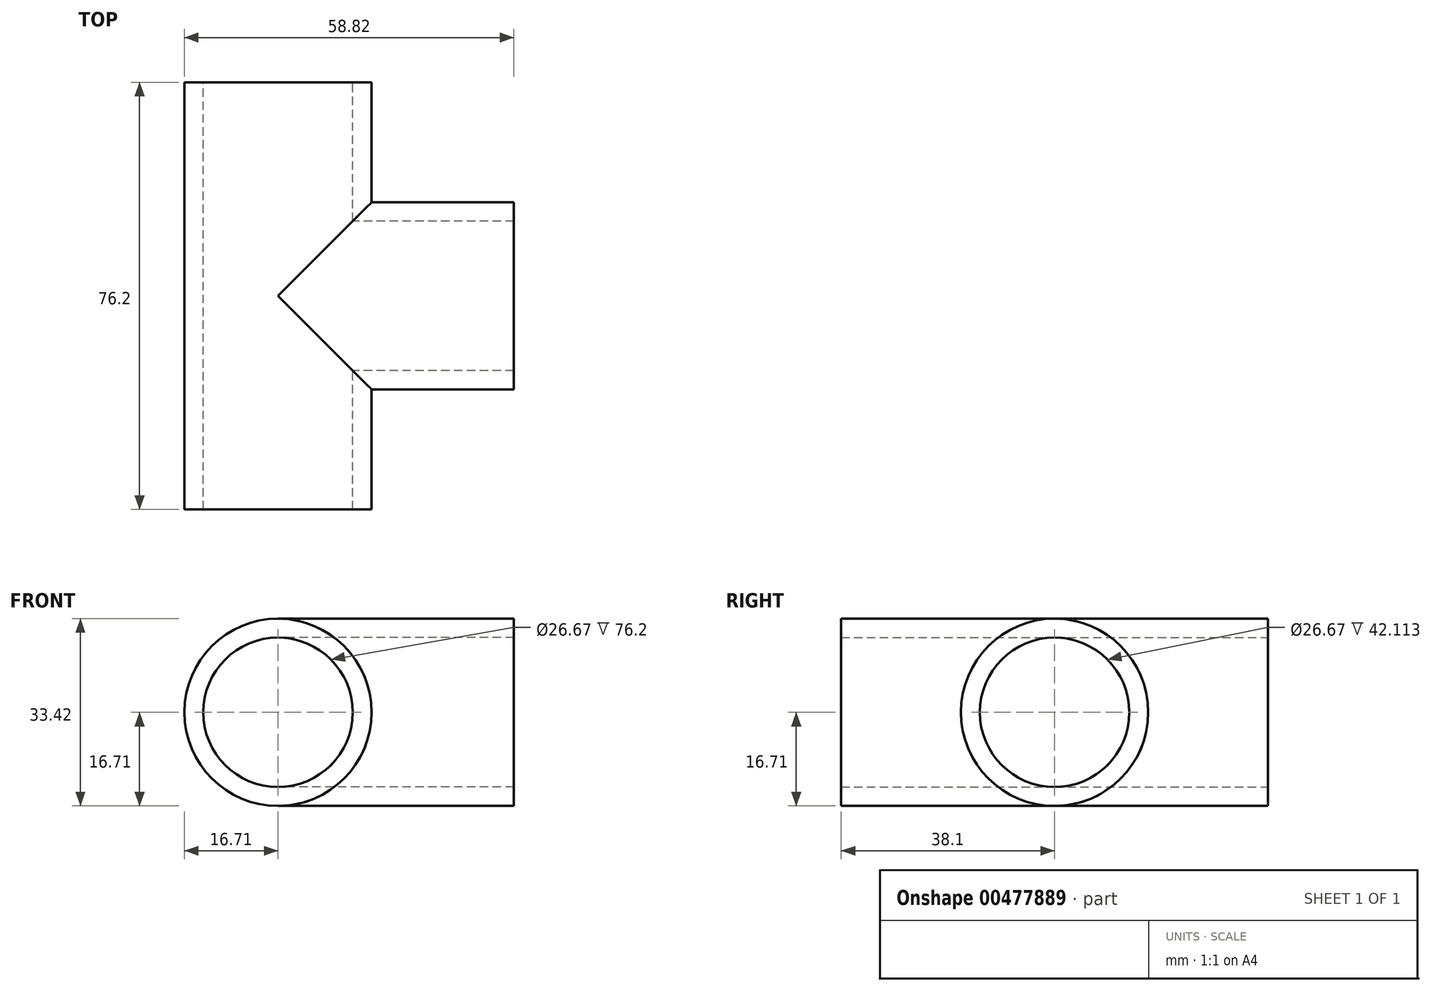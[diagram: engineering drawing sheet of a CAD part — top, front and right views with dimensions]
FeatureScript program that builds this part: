
annotation { "Feature Type Name" : "Feature", "Feature Type Description" : "" }
export const myFeature = defineFeature(function(context is Context, id is Id, definition is map)
    precondition{}
    {
        {
            var Q0;
            Q0=qCreatedBy(makeId("Top.planeOp"),FACE);
            var sketch = newSketch(context, id + "F0", { "sketchPlane" : qUnion([Q0])});
            skLineSegment(sketch, "E0", {"start": v(0, 38.1) * mm, "end": v(0, 0) * mm});
            skLineSegment(sketch, "E1", {"start": v(0, 0) * mm, "end": v(0, -38.1) * mm});
            skLineSegment(sketch, "E2", {"start": v(0, 0) * mm, "end": v(42.11, 0) * mm});
            skLineSegment(sketch, "E3", {"start": v(42.11, 0) * mm, "end": v(42.11, 16.71) * mm});
            skLineSegment(sketch, "E4", {"start": v(42.11, 16.71) * mm, "end": v(16.71, 16.71) * mm});
            skLineSegment(sketch, "E5", {"start": v(16.71, 16.71) * mm, "end": v(16.71, 38.1) * mm});
            skLineSegment(sketch, "E6", {"start": v(16.71, 38.1) * mm, "end": v(-16.71, 38.1) * mm});
            skLineSegment(sketch, "E7", {"start": v(-16.71, 38.1) * mm, "end": v(-16.71, -38.1) * mm});
            skLineSegment(sketch, "E8", {"start": v(-16.71, -38.1) * mm, "end": v(16.71, -38.1) * mm});
            skLineSegment(sketch, "E9", {"start": v(16.71, -38.1) * mm, "end": v(16.71, -16.71) * mm});
            skLineSegment(sketch, "E10", {"start": v(16.71, -16.71) * mm, "end": v(42.11, -16.71) * mm});
            skLineSegment(sketch, "E11", {"start": v(42.11, -16.71) * mm, "end": v(42.11, 0) * mm});
            skLineSegment(sketch, "E12", {"start": v(16.71, 16.71) * mm, "end": v(0, 16.71) * mm});
            skPoint(sketch, "E12.endSnap0", {"position": v(0, 19.05) * mm});
            skLineSegment(sketch, "E13", {"start": v(16.71, -16.71) * mm, "end": v(0, -16.71) * mm});
            skLineSegment(sketch, "E14", {"start": v(0, 16.71) * mm, "end": v(-16.71, 16.71) * mm, "construction": true});
            skLineSegment(sketch, "E15", {"start": v(42.11, 13.33) * mm, "end": v(3.29, 13.33) * mm});
            skLineSegment(sketch, "E16", {"start": v(42.11, -13.34) * mm, "end": v(3.29, -13.34) * mm});
            skLineSegment(sketch, "E17", {"start": v(-13.33, -38.1) * mm, "end": v(-13.33, 38.1) * mm});
            skLineSegment(sketch, "E18", {"start": v(3.29, 13.33) * mm, "end": v(0, 13.33) * mm});
            skLineSegment(sketch, "E19", {"start": v(3.29, -13.34) * mm, "end": v(0, -13.34) * mm});
            skLineSegment(sketch, "E20", {"start": v(13.34, 16.71) * mm, "end": v(13.34, 38.1) * mm, "construction": true});
            skLineSegment(sketch, "E21", {"start": v(13.34, -16.71) * mm, "end": v(13.34, -38.1) * mm, "construction": true});
            skLineSegment(sketch, "E22", {"start": v(13.34, -27.4) * mm, "end": v(16.71, -27.4) * mm, "construction": true});
            skLineSegment(sketch, "E23", {"start": v(16.71, 27.4) * mm, "end": v(13.33, 27.4) * mm, "construction": true});
            skLineSegment(sketch, "E24", {"start": v(-13.33, 27.4) * mm, "end": v(-16.71, 27.4) * mm, "construction": true});
            skLineSegment(sketch, "E25", {"start": v(29.41, 16.71) * mm, "end": v(29.41, 13.33) * mm, "construction": true});
            skLineSegment(sketch, "E26", {"start": v(29.41, -16.71) * mm, "end": v(29.41, -13.33) * mm, "construction": true});
            skSolve(sketch);
        }
        {
            var Q0;
            {var subQ0=sQuery(id+"F0.wireOp",EDGE,"E7");Q0=makeQuery(id+"F0.imprint","IMPRINT",FACE,{"disambiguationData":[TD([[makeQuery(id+"F0.imprint","IMPRINT",EDGE,{"derivedFrom":subQ0}),1.0]])]});}
            var Q1;
            Q1=sQuery(id+"F0.wireOp",EDGE,"E0");
            revolve(context, id + "F1", {"entities" : qUnion([Q0]), "axis" : qUnion([Q1]), "revolveType" : RevolveType.FULL});
        }
        {
            var Q0;
            {var subQ1=sQuery(id+"F0.wireOp",EDGE,"E4");Q0=makeQuery(id+"F0.imprint","IMPRINT",FACE,{"disambiguationData":[TD([[makeQuery(id+"F0.imprint","IMPRINT",EDGE,{"derivedFrom":subQ1}),1.0]])]});}
            var Q1;
            Q1=sQuery(id+"F0.wireOp",EDGE,"E2");
            revolve(context, id + "F2", {"operationType" : NewBodyOperationType.ADD, "entities" : qUnion([Q0]), "axis" : qUnion([Q1]), "revolveType" : RevolveType.FULL});
        }
        {
            var Q0;
            Q0=makeQuery(id+"F2.opRevolve","SWEPT_FACE",FACE,{"disambiguationData":[OSD([sQuery(id+"F0.wireOp",EDGE,"E3")])]});
            var sketch = newSketch(context, id + "F3", { "sketchPlane" : qUnion([Q0])});
            skSolve(sketch);
        }
        {
            var Q0;
            Q0=makeQuery(id+"F1.opRevolve","SWEPT_FACE",FACE,{"disambiguationData":[OSD([sQuery(id+"F0.wireOp",EDGE,"E8")])]});
            var sketch = newSketch(context, id + "F4", { "sketchPlane" : qUnion([Q0])});
            skSolve(sketch);
        }
        {
            var Q0;
            Q0=makeQuery(id+"F4.imprint","IMPRINT",FACE,{"disambiguationData":[TD([[makeQuery(id+"F4.imprint","IMPRINT",EDGE,{"derivedFrom":makeQuery(id+"F1.opRevolve","SWEPT_EDGE",EDGE,{"disambiguationData":[OSD([sQuery(id+"F0.wireOp",EDGE,"E8"),sQuery(id+"F0.wireOp",EDGE,"E17")])]})}),-1.0]])]});
            extrude(context, id + "F5", {"entities" : qUnion([Q0]), "operationType" : NewBodyOperationType.REMOVE, "endBound" : BoundingType.THROUGH_ALL, "oppositeDirection" : true, "depth" : 25.4 * mm});
        }
        {
            var Q0;
            Q0=makeQuery(id+"F3.imprint","IMPRINT",FACE,{"disambiguationData":[TD([[makeQuery(id+"F3.imprint","IMPRINT",EDGE,{"derivedFrom":makeQuery(id+"F2.opRevolve","SWEPT_EDGE",EDGE,{"disambiguationData":[OSD([sQuery(id+"F0.wireOp",EDGE,"E3"),sQuery(id+"F0.wireOp",EDGE,"E15")])]})}),-1.0]])]});
            var Q1;
            Q1=sQuery(id+"F0.wireOp",VERTEX,"E2.start");
            extrude(context, id + "F6", {"entities" : qUnion([Q0]), "operationType" : NewBodyOperationType.REMOVE, "endBound" : BoundingType.UP_TO_VERTEX, "oppositeDirection" : true, "endBoundEntityVertex" : qUnion([Q1]), "depth" : 25.4 * mm});
        }
    });
